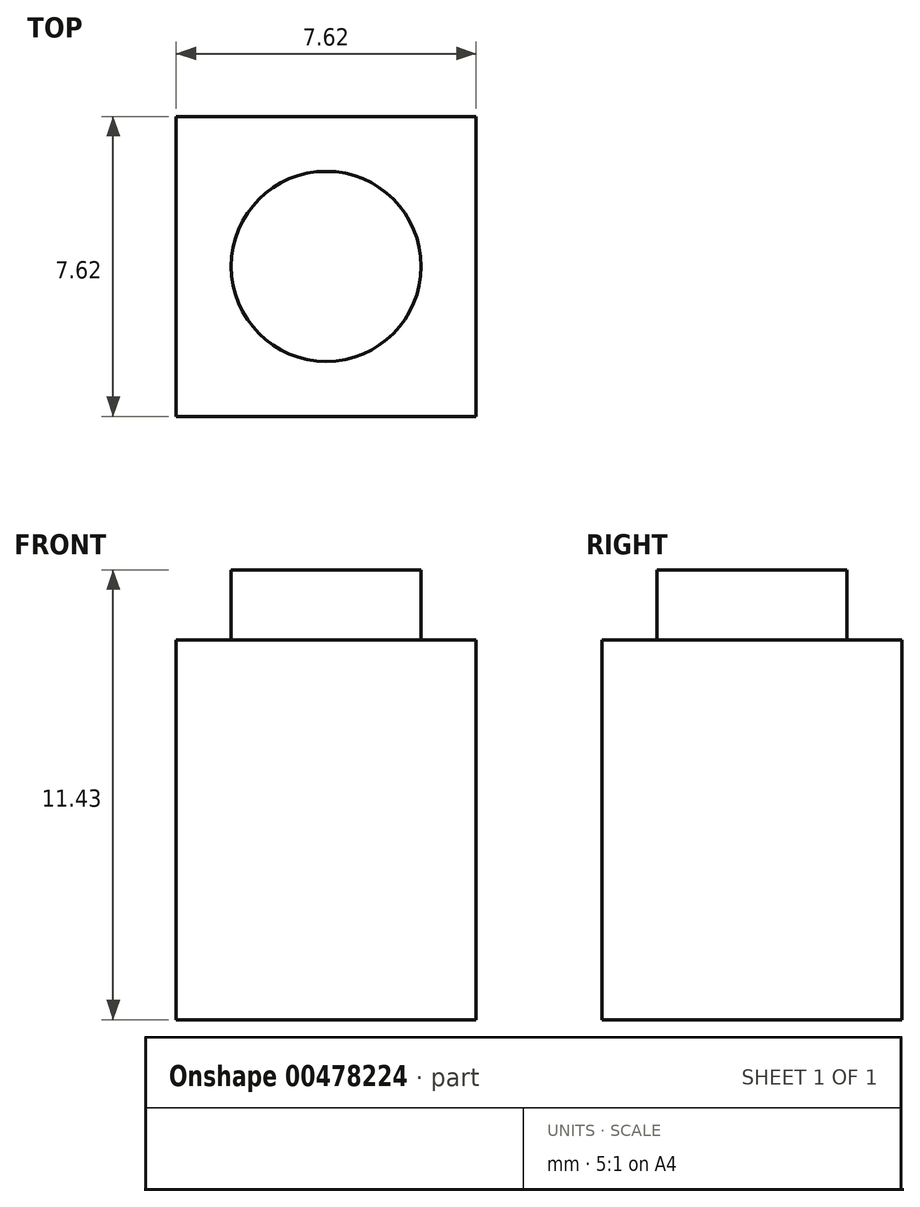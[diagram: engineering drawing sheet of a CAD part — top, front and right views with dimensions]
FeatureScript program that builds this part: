
annotation { "Feature Type Name" : "Feature", "Feature Type Description" : "" }
export const myFeature = defineFeature(function(context is Context, id is Id, definition is map)
    precondition{}
    {
        {
            var Q0;
            Q0=qCreatedBy(makeId("Top.planeOp"),FACE);
            var sketch = newSketch(context, id + "F0", { "sketchPlane" : qUnion([Q0])});
            skLineSegment(sketch, "E0.bottom", {"start": v(-3.81, 3.8) * mm, "end": v(3.81, 3.8) * mm});
            skLineSegment(sketch, "E0.top", {"start": v(-3.81, -3.81) * mm, "end": v(3.8, -3.81) * mm});
            skLineSegment(sketch, "E0.left", {"start": v(-3.8, 3.8) * mm, "end": v(-3.81, -3.81) * mm});
            skLineSegment(sketch, "E0.right", {"start": v(3.81, 3.8) * mm, "end": v(3.8, -3.81) * mm});
            skPoint(sketch, "E0.middle", {"position": v(0, 0) * mm});
            skSolve(sketch);
        }
        {
            var Q0;
            Q0 = qSketchRegion(id + "F0", true);
            extrude(context, id + "F1", {"entities" : qUnion([Q0]), "depth" : 9.65 * mm, "offsetDistance" : 25.4 * mm});
        }
        {
            var Q0;
            Q0=makeQuery(id+"F1.opExtrude","CAP_FACE",FACE,{"disambiguationData":[OSD([sQuery(id+"F0.wireOp",EDGE,"E0.bottom"),sQuery(id+"F0.wireOp",EDGE,"E0.top"),sQuery(id+"F0.wireOp",EDGE,"E0.left"),sQuery(id+"F0.wireOp",EDGE,"E0.right")])],"isStart":false});
            var sketch = newSketch(context, id + "F2", { "sketchPlane" : qUnion([Q0])});
            skCircle(sketch, "E1", {"center": v(0, 0) * mm, "radius": 2.41 * mm});
            skSolve(sketch);
        }
        {
            var Q0;
            Q0 = qSketchRegion(id + "F2", true);
            extrude(context, id + "F3", {"entities" : qUnion([Q0]), "operationType" : NewBodyOperationType.ADD, "depth" : 1.78 * mm, "offsetDistance" : 25.4 * mm});
        }
    });
